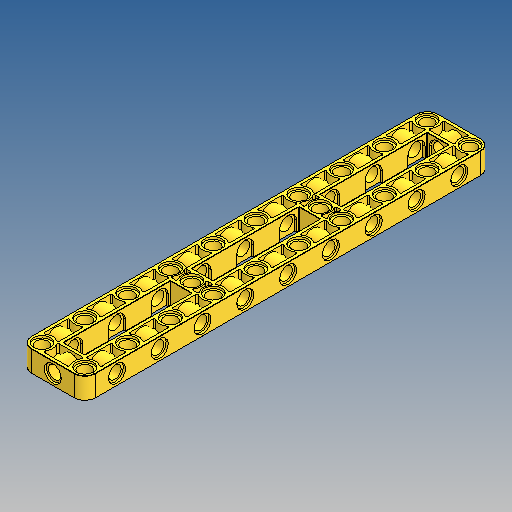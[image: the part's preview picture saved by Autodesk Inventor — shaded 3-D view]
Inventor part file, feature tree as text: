
AUTODESK INVENTOR PART (.ipt)
format: ipt  version: 2025 (Build 290162010, 162A)  size: 1,366,528 bytes
history: native  units: mm
features: extrude x17, sketch x14, mirror x3, fillet x1, projected_geometry x1
ambient origin geometry x8: Origin, YZ Plane, XZ Plane, XY Plane, X Axis, Y Axis, Z Axis, Center Point
bodies: Solid1 (feature_tree)
feature tree (36):
  extrude  "Extrusion1"  Depth=0.8mm TaperAngle=0.0deg
  sketch  "Sketch6"  dims[d49=6.4mm d50=4.8mm]
  extrude  "Extrusion7"  Depth=48.0mm
  extrude  "Extrusion8"  Depth=6.4mm
  extrude  "Extrusion19"  Depth=0.4mm
  mirror  "Mirror5"
  sketch  "Sketch7"  dims[d51=16.0mm d60=0.4mm d61=0.1mm]
  extrude  "Extrusion9"  Depth=7.2mm
  extrude  "Extrusion10"  Depth=10.0mm TaperAngle=0.0deg
  extrude  "Extrusion11"  Depth=6.4mm
  extrude  "Extrusion18"  Depth=6.4mm
  extrude  "Extrusion20"  TaperAngle=0.0deg  [1 undecoded]
  extrude  "Extrusion27"  Depth=1.6mm
  extrude  "Extrusion28"  Depth=16.0mm
  extrude  "Extrusion21"  Depth=56.0mm
  sketch  "Skizze18"  dims[d112=3.1mm d113=0.0mm d114=16.0mm]
  extrude  "Extrusion22"  Depth=16.0mm
  extrude  "Extrusion23"  Depth=8.0mm
  fillet  "Fillet2"  Radius=0.8mm
  sketch  "Sketch12"  dims[d70=4.8mm d71=10.0mm d72=0.0mm]
  extrude  "Extrusion24"  Depth=1.6mm
  extrude  "Extrusion25"  Depth=1.172mm
  extrude  "Extrusion26"  Depth=10.0mm TaperAngle=0.0deg
  mirror  "Mirror4"
  mirror  "Mirror3"
  sketch  "Sketch1"  dims[d14=8.0mm d15=0.0mm d41=0.8mm d42=0.0mm]
  projected_geometry  "Projected Loop4"
  sketch  "Skizze - Rechteckige Anordnung1"  dims[d43=3.1mm d44=0.0mm d48=48.0mm]
  sketch  "Sketch8"  dims[d62=30.0mm d64=16.0mm d65=10.0mm d67=10.0mm d69=7.2mm]
  sketch  "Sketch14"  dims[d73=10.0mm d74=0.0mm d75=6.4mm]
  sketch  "Sketch15"  dims[d76=0.8mm d77=0.0mm d106=6.4mm]
  sketch  "Skizze16"  dims[d107=0.8mm d108=0.0mm]
  sketch  "Skizze17"  dims[d109=45.0deg d111=1.6mm]
  sketch  "Skizze19"  dims[d116=45.0deg d117=56.0mm]
  sketch  "Skizze20"  dims[d118=8.0mm d119=16.0mm]
  sketch  "Skizze21"  dims[d120=16.0mm d121=8.0mm d122=0.8mm d123=0.0mm d124=1.6mm d125=1.172mm d126=10.0mm d127=0.0mm d128=1.172mm d129=0.4mm d131=0.0mm d132=0.0mm d133=6.4mm d134=8.0mm d135=3.2mm d136=0.8mm d137=0.0mm d138=7.2mm d139=4.8mm d140=6.4mm d141=0.0mm d142=10.0mm d143=0.0mm d144=0.8mm d145=0.0mm d146=10.0mm d147=0.0mm d148=10.0mm d149=0.0mm d150=1.172mm d151=1.172mm d152=0.6mm d153=0.4mm]
note: 1 required parameter value undecoded (feature->parameter linkage not recoverable at this tier; creation-order binding heuristic only, values carry confidence <= 0.55)
